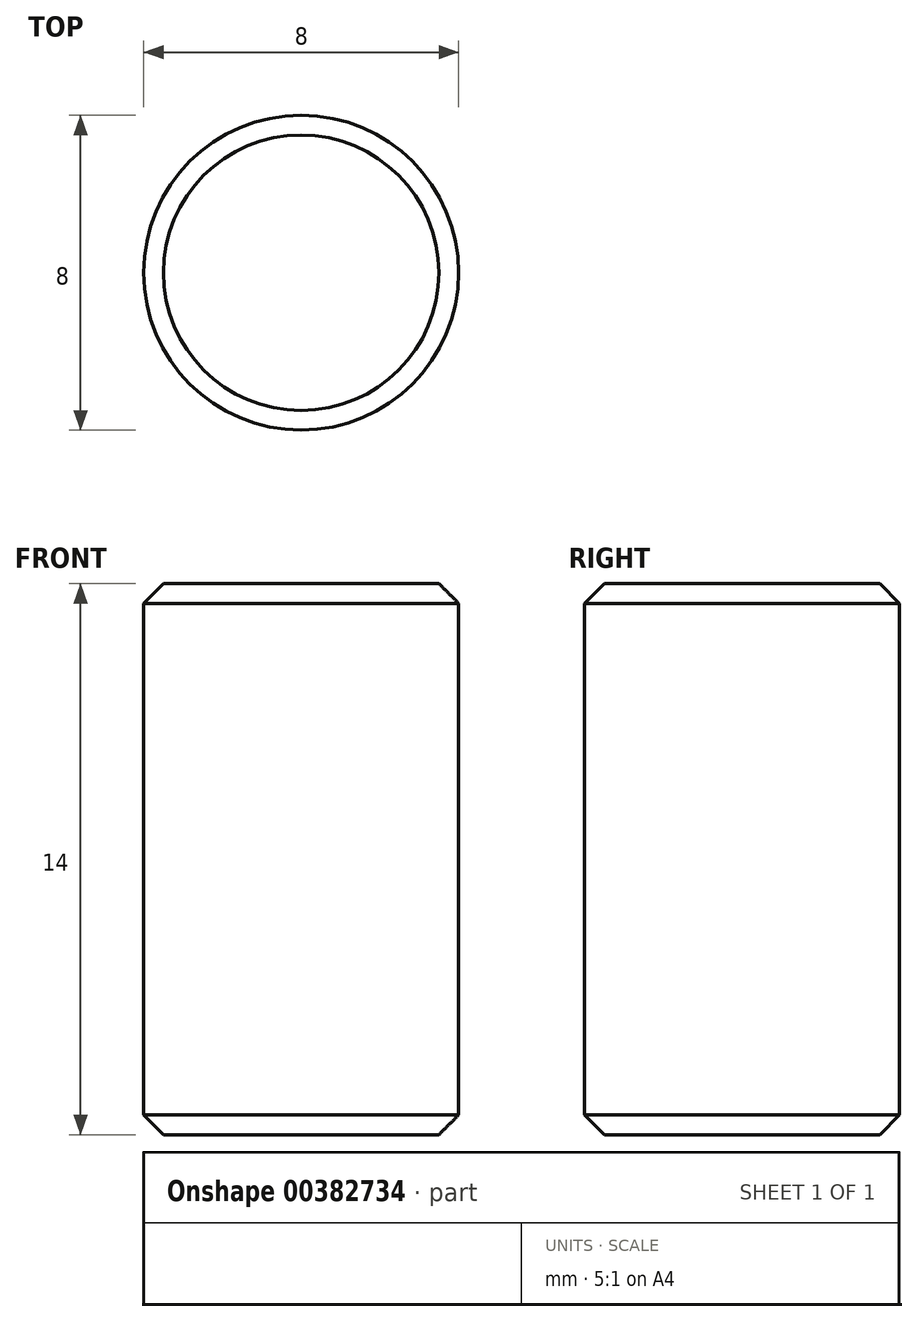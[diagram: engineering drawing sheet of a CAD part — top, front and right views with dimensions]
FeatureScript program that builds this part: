
annotation { "Feature Type Name" : "Feature", "Feature Type Description" : "" }
export const myFeature = defineFeature(function(context is Context, id is Id, definition is map)
    precondition{}
    {
        {
            var Q0;
            Q0=qCreatedBy(makeId("Top.planeOp"),FACE);
            var sketch = newSketch(context, id + "F0", { "sketchPlane" : qUnion([Q0])});
            skCircle(sketch, "E0", {"center": v(0, 0) * mm, "radius": 4 * mm});
            skCircle(sketch, "E1", {"center": v(0, 0) * mm, "radius": 6 * mm});
            skSolve(sketch);
        }
        {
            var Q0;
            Q0=makeQuery(id+"F0.imprint","IMPRINT",FACE,{"disambiguationData":[TD([[makeQuery(id+"F0.imprint","IMPRINT",EDGE,{"derivedFrom":sQuery(id+"F0.wireOp",EDGE,"E0")}),1.0]])]});
            extrude(context, id + "F1", {"entities" : qUnion([Q0]), "depth" : 14 * mm});
        }
        {
            var Q0;
            Q0=makeQuery(id+"F1.opExtrude","SWEPT_FACE",FACE,{"disambiguationData":[OSD([sQuery(id+"F0.wireOp",EDGE,"E0")])]});
            chamfer(context, id + "F2", {"entities" : qUnion([Q0]), "width" : 0.5 * mm, "tangentPropagation" : true});
        }
    });
